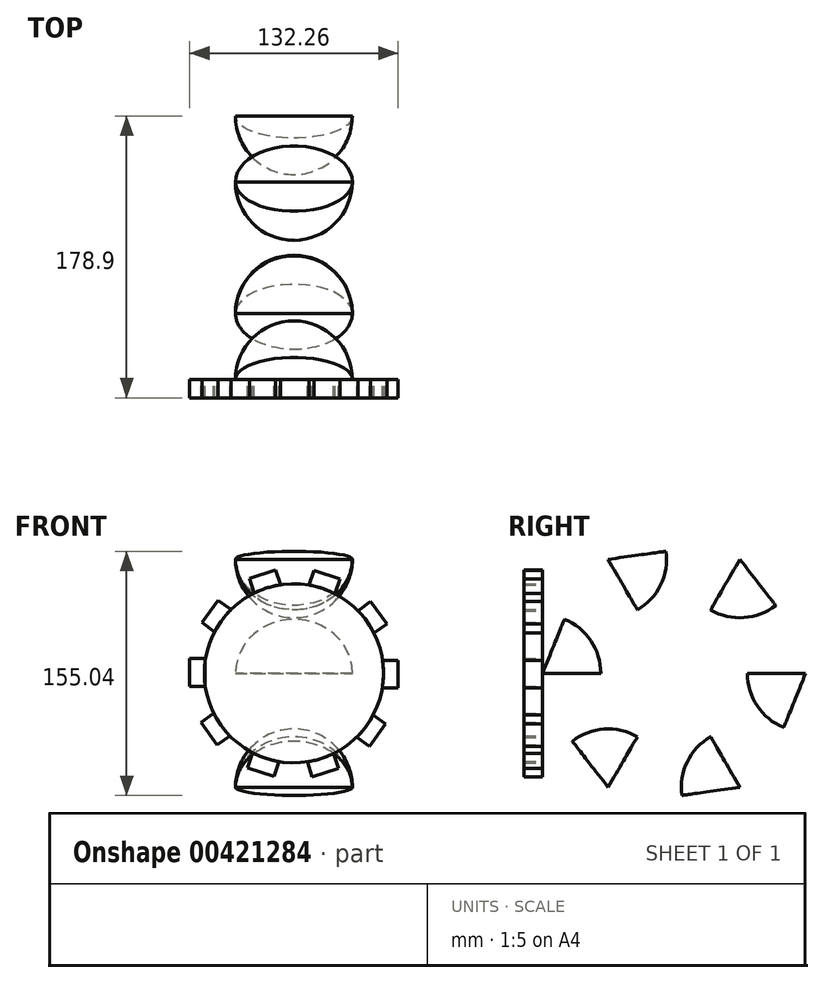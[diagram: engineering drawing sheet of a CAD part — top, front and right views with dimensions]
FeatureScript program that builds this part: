
annotation { "Feature Type Name" : "Feature", "Feature Type Description" : "" }
export const myFeature = defineFeature(function(context is Context, id is Id, definition is map)
    precondition{}
    {
        {
            var Q0;
            Q0=qCreatedBy(makeId("Top.planeOp"),FACE);
            var sketch = newSketch(context, id + "F0", { "sketchPlane" : qUnion([Q0])});
            skArc(sketch, "E0", {"start": v(37.1, 0) * mm, "mid": v(0, 37.1) * mm, "end": v(-37.1, 0) * mm});
            skLineSegment(sketch, "E1", {"start": v(-37.1, 0) * mm, "end": v(37.1, 0) * mm});
            skSolve(sketch);
        }
        {
            var Q0;
            Q0=makeQuery(id+"F0.imprint","IMPRINT",FACE,{"disambiguationData":[TD([[makeQuery(id+"F0.imprint","IMPRINT",EDGE,{"derivedFrom":sQuery(id+"F0.wireOp",EDGE,"E0")}),1.0]])]});
            var Q1;
            Q1=sQuery(id+"F0.wireOp",EDGE,"E1");
            revolve(context, id + "F1", {"entities" : qUnion([Q0]), "axis" : qUnion([Q1]), "revolveType" : RevolveType.ONE_DIRECTION, "angle" : 67.93 * degree});
        }
        {
            var Q0;
            Q0=qCreatedBy(makeId("Top.planeOp"),FACE);
            var sketch = newSketch(context, id + "F2", { "sketchPlane" : qUnion([Q0])});
            skLineSegment(sketch, "E2", {"start": v(53.4, 83.6) * mm, "end": v(131.46, 83.6) * mm});
            skSolve(sketch);
        }
        {
            var Q0;
            Q0=makeQuery(id+"F1.opRevolve","SWEPT_BODY",BODY,{"disambiguationData":[OSD([sQuery(id+"F0.wireOp",EDGE,"E0"),sQuery(id+"F0.wireOp",EDGE,"E1")])]});
            var Q1;
            Q1=sQuery(id+"F2.wireOp",EDGE,"E2");
            circularPattern(context, id + "F3", {"entities" : qUnion([Q0]), "axis" : qUnion([Q1]), "angle" : 360 * degree, "instanceCount" : 6, "equalSpace" : true});
        }
        {
            var Q0;
            Q0=qCreatedBy(makeId("Front.planeOp"),FACE);
            var sketch = newSketch(context, id + "F4", { "sketchPlane" : qUnion([Q0])});
            skCircle(sketch, "E3", {"center": v(0, 0) * mm, "radius": 56.87 * mm});
            skLineSegment(sketch, "E4.bottom", {"start": v(-56.27, -8.2) * mm, "end": v(-66.13, -8.2) * mm});
            skLineSegment(sketch, "E4.top", {"start": v(-56.27, 9.34) * mm, "end": v(-66.13, 9.34) * mm});
            skLineSegment(sketch, "E4.left", {"start": v(-56.27, -8.2) * mm, "end": v(-56.27, 9.34) * mm});
            skLineSegment(sketch, "E4.right", {"start": v(-66.13, -8.2) * mm, "end": v(-66.13, 9.34) * mm});
            skSolve(sketch);
        }
        {
            var Q0;
            {var subQ0=sQuery(id+"F4.wireOp",EDGE,"E4.left");var subQ1=sQuery(id+"F4.wireOp",EDGE,"E3");var subQ3=makeQuery(id+"F4.imprint","INTERSECT",VERTEX,{"derivedFrom":[subQ1,subQ0]});Q0=makeQuery(id+"F4.imprint","IMPRINT",FACE,{"disambiguationData":[TD([[makeQuery(id+"F4.imprint","IMPRINT",EDGE,{"disambiguationData":[TD([[subQ3,1.0]])],"derivedFrom":subQ1}),1.0]])]});}
            var Q1;
            {var subQ1=sQuery(id+"F4.wireOp",EDGE,"E4.bottom");Q1=makeQuery(id+"F4.imprint","IMPRINT",FACE,{"disambiguationData":[TD([[makeQuery(id+"F4.imprint","IMPRINT",EDGE,{"derivedFrom":subQ1}),-1.0]])]});}
            extrude(context, id + "F5", {"entities" : qUnion([Q0, Q1]), "depth" : 11.68 * mm});
        }
        {
            var Q0;
            Q0=qCreatedBy(makeId("Top.planeOp"),FACE);
            var sketch = newSketch(context, id + "F6", { "sketchPlane" : qUnion([Q0])});
            skLineSegment(sketch, "E5", {"start": v(0, 3.33) * mm, "end": v(0, -53.34) * mm});
            skSolve(sketch);
        }
        {
            var Q0;
            Q0=makeQuery(id+"F5.opExtrude","SWEPT_BODY",BODY,{"disambiguationData":[OSD([sQuery(id+"F4.wireOp",EDGE,"E3"),sQuery(id+"F4.wireOp",EDGE,"E4.bottom"),sQuery(id+"F4.wireOp",EDGE,"E4.top"),sQuery(id+"F4.wireOp",EDGE,"E4.left"),sQuery(id+"F4.wireOp",EDGE,"E4.right")])]});
            var Q1;
            Q1=sQuery(id+"F6.wireOp",EDGE,"E5");
            circularPattern(context, id + "F7", {"entities" : qUnion([Q0]), "axis" : qUnion([Q1]), "angle" : 360 * degree, "instanceCount" : 10, "equalSpace" : true});
        }
    });
